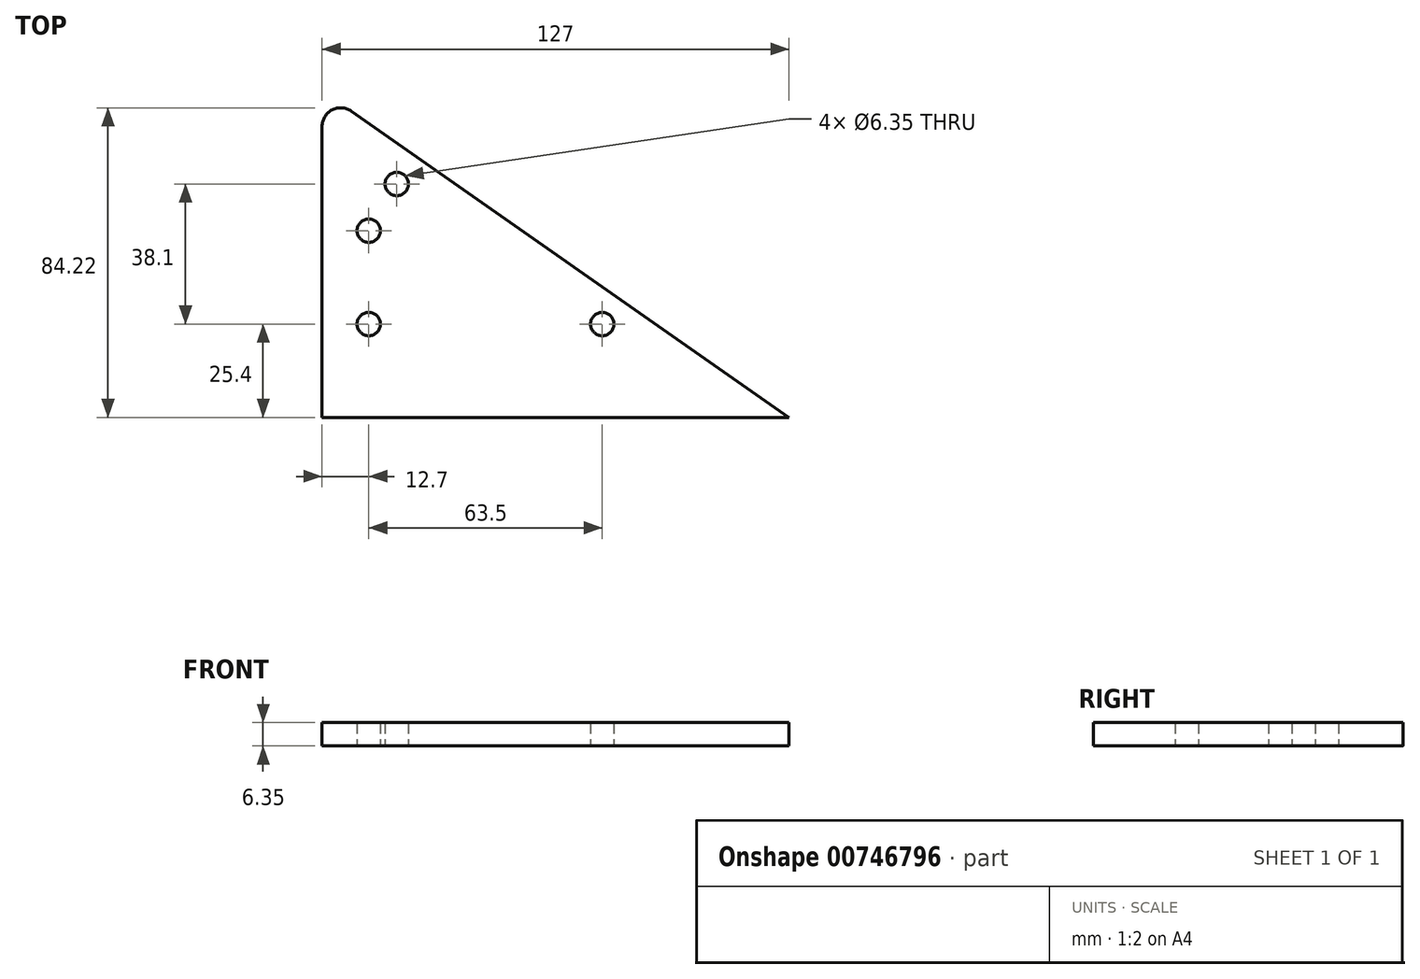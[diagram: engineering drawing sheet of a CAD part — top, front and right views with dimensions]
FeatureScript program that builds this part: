
annotation { "Feature Type Name" : "Feature", "Feature Type Description" : "" }
export const myFeature = defineFeature(function(context is Context, id is Id, definition is map)
    precondition{}
    {
        {
            var Q0;
            Q0=qCreatedBy(makeId("Top.planeOp"),FACE);
            var sketch = newSketch(context, id + "F0", { "sketchPlane" : qUnion([Q0])});
            skLineSegment(sketch, "E0", {"start": v(0, 79.14) * mm, "end": v(0, 0) * mm});
            skLineSegment(sketch, "E1", {"start": v(0, 0) * mm, "end": v(127, 0) * mm});
            skLineSegment(sketch, "E2", {"start": v(127, 0) * mm, "end": v(8, 83.3) * mm});
            skCircle(sketch, "E3", {"center": v(12.7, 25.4) * mm, "radius": 3.18 * mm});
            skCircle(sketch, "E4", {"center": v(76.2, 25.4) * mm, "radius": 3.18 * mm});
            skCircle(sketch, "E5", {"center": v(12.7, 50.8) * mm, "radius": 3.18 * mm});
            skCircle(sketch, "E6", {"center": v(20.32, 63.5) * mm, "radius": 3.18 * mm});
            skPoint(sketch, "E7.visualSharp", {"position": v(0, 88.9) * mm});
            skArc(sketch, "E7.filletArc", {"start": v(8, 83.3) * mm, "mid": v(2.73, 83.65) * mm, "end": v(0, 79.14) * mm});
            skSolve(sketch);
        }
        {
            var Q0;
            Q0=makeQuery(id+"F0.imprint","IMPRINT",FACE,{"disambiguationData":[TD([[makeQuery(id+"F0.imprint","IMPRINT",EDGE,{"derivedFrom":sQuery(id+"F0.wireOp",EDGE,"E0")}),1.0]])]});
            extrude(context, id + "F1", {"entities" : qUnion([Q0]), "depth" : 6.35 * mm, "offsetDistance" : 25.4 * mm});
        }
    });
